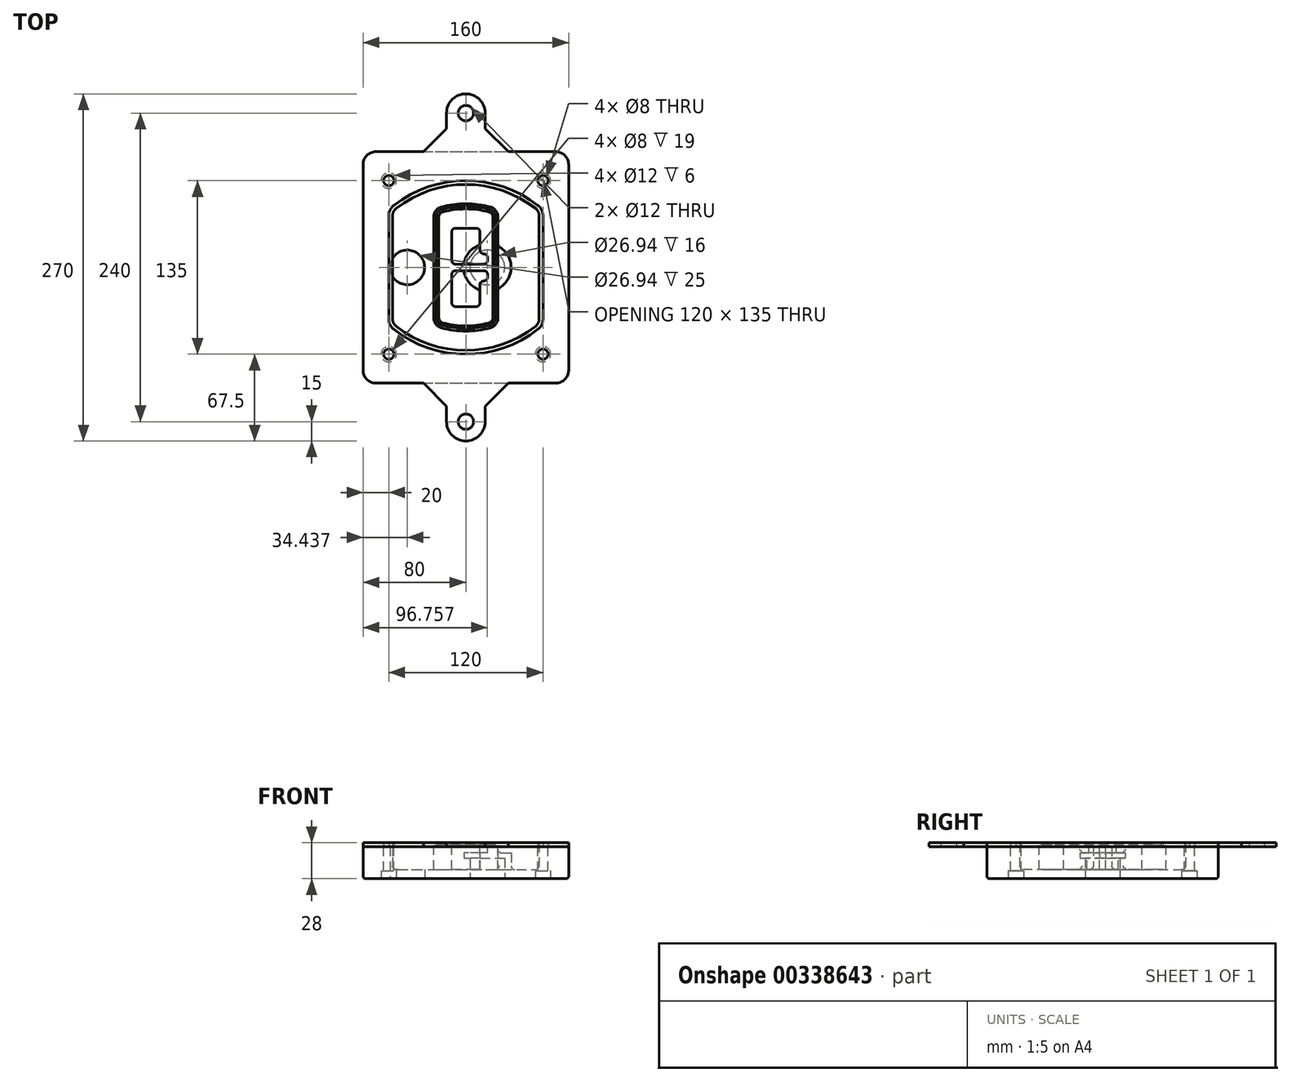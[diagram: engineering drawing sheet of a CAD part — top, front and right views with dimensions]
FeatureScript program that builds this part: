
annotation { "Feature Type Name" : "Feature", "Feature Type Description" : "" }
export const myFeature = defineFeature(function(context is Context, id is Id, definition is map)
    precondition{}
    {
        {
            var Q0;
            Q0=qCreatedBy(makeId("Top.planeOp"),FACE);
            var sketch = newSketch(context, id + "F0", { "sketchPlane" : qUnion([Q0])});
            skPoint(sketch, "E0.rect.middle", {"position": v(0, 0) * mm});
            skLineSegment(sketch, "E1.bottom", {"start": v(-70, -90) * mm, "end": v(70, -90) * mm});
            skLineSegment(sketch, "E1.top", {"start": v(-70, 90) * mm, "end": v(70, 90) * mm});
            skLineSegment(sketch, "E1.left", {"start": v(-80, -80) * mm, "end": v(-80, 80) * mm});
            skLineSegment(sketch, "E1.right", {"start": v(80, -80) * mm, "end": v(80, 80) * mm});
            skLineSegment(sketch, "E2", {"start": v(-80, 90) * mm, "end": v(80, -90) * mm, "construction": true});
            skLineSegment(sketch, "E3", {"start": v(80, 90) * mm, "end": v(-80, -90) * mm, "construction": true});
            skCircle(sketch, "E4", {"center": v(-60, 67.5) * mm, "radius": 4 * mm});
            skCircle(sketch, "E5", {"center": v(60, 67.5) * mm, "radius": 4 * mm});
            skCircle(sketch, "E6", {"center": v(60, -67.5) * mm, "radius": 4 * mm});
            skCircle(sketch, "E7", {"center": v(-60, -67.5) * mm, "radius": 4 * mm});
            skLineSegment(sketch, "E8", {"start": v(-60, 67.5) * mm, "end": v(60, 67.5) * mm, "construction": true});
            skLineSegment(sketch, "E9", {"start": v(60, 67.5) * mm, "end": v(60, -67.5) * mm, "construction": true});
            skLineSegment(sketch, "E10", {"start": v(60, -67.5) * mm, "end": v(-60, -67.5) * mm, "construction": true});
            skLineSegment(sketch, "E11", {"start": v(-60, -67.5) * mm, "end": v(-60, 67.5) * mm, "construction": true});
            skLineSegment(sketch, "E12", {"start": v(-60, 40.3) * mm, "end": v(-60, -40.3) * mm});
            skLineSegment(sketch, "E13", {"start": v(60, 40.3) * mm, "end": v(60, -40.3) * mm});
            skArc(sketch, "E14", {"start": v(56.15, 48.18) * mm, "mid": v(0, 67.5) * mm, "end": v(-56.15, 48.18) * mm});
            skArc(sketch, "E15", {"start": v(-56.15, -48.18) * mm, "mid": v(0, -67.5) * mm, "end": v(56.15, -48.18) * mm});
            skLineSegment(sketch, "E16", {"start": v(-60, 0) * mm, "end": v(60, 0) * mm, "construction": true});
            skPoint(sketch, "E17.visualSharp", {"position": v(-60, -45) * mm});
            skArc(sketch, "E17.filletArc", {"start": v(-60, -40.3) * mm, "mid": v(-58.99, -44.68) * mm, "end": v(-56.15, -48.18) * mm});
            skPoint(sketch, "E18.visualSharp", {"position": v(-60, 45) * mm});
            skArc(sketch, "E18.filletArc", {"start": v(-56.15, 48.18) * mm, "mid": v(-58.99, 44.68) * mm, "end": v(-60, 40.3) * mm});
            skPoint(sketch, "E19.visualSharp", {"position": v(60, 45) * mm});
            skArc(sketch, "E19.filletArc", {"start": v(60, 40.3) * mm, "mid": v(58.99, 44.68) * mm, "end": v(56.15, 48.18) * mm});
            skPoint(sketch, "E20.visualSharp", {"position": v(60, -45) * mm});
            skArc(sketch, "E20.filletArc", {"start": v(56.15, -48.18) * mm, "mid": v(58.99, -44.68) * mm, "end": v(60, -40.3) * mm});
            skPoint(sketch, "E21.visualSharp", {"position": v(-80, 90) * mm});
            skArc(sketch, "E21.filletArc", {"start": v(-70, 90) * mm, "mid": v(-77.07, 87.07) * mm, "end": v(-80, 80) * mm});
            skPoint(sketch, "E22.visualSharp", {"position": v(80, 90) * mm});
            skArc(sketch, "E22.filletArc", {"start": v(80, 80) * mm, "mid": v(77.07, 87.07) * mm, "end": v(70, 90) * mm});
            skPoint(sketch, "E23.visualSharp", {"position": v(80, -90) * mm});
            skArc(sketch, "E23.filletArc", {"start": v(70, -90) * mm, "mid": v(77.07, -87.07) * mm, "end": v(80, -80) * mm});
            skPoint(sketch, "E24.visualSharp", {"position": v(-80, -90) * mm});
            skArc(sketch, "E24.filletArc", {"start": v(-80, -80) * mm, "mid": v(-77.07, -87.07) * mm, "end": v(-70, -90) * mm});
            skArc(sketch, "E25.0", {"start": v(57, 40.3) * mm, "mid": v(56.3, 43.36) * mm, "end": v(54.3, 45.81) * mm});
            skLineSegment(sketch, "E25.1", {"start": v(57, 40.3) * mm, "end": v(57, -40.3) * mm});
            skArc(sketch, "E25.2", {"start": v(54.3, -45.81) * mm, "mid": v(56.3, -43.36) * mm, "end": v(57, -40.3) * mm});
            skArc(sketch, "E25.3", {"start": v(-54.3, -45.81) * mm, "mid": v(0, -64.5) * mm, "end": v(54.3, -45.81) * mm});
            skArc(sketch, "E25.4", {"start": v(-57, -40.3) * mm, "mid": v(-56.3, -43.36) * mm, "end": v(-54.3, -45.81) * mm});
            skArc(sketch, "E25.5", {"start": v(54.3, 45.81) * mm, "mid": v(0, 64.5) * mm, "end": v(-54.3, 45.81) * mm});
            skLineSegment(sketch, "E25.6", {"start": v(-57, 40.3) * mm, "end": v(-57, -40.3) * mm});
            skArc(sketch, "E25.7", {"start": v(-54.3, 45.81) * mm, "mid": v(-56.3, 43.36) * mm, "end": v(-57, 40.3) * mm});
            skArc(sketch, "E26.0", {"start": v(-58.62, 51.33) * mm, "mid": v(-62.58, 46.43) * mm, "end": v(-64, 40.3) * mm});
            skArc(sketch, "E26.1", {"start": v(58.62, 51.33) * mm, "mid": v(0, 71.5) * mm, "end": v(-58.62, 51.33) * mm});
            skArc(sketch, "E26.2", {"start": v(64, 40.3) * mm, "mid": v(62.58, 46.43) * mm, "end": v(58.62, 51.33) * mm});
            skLineSegment(sketch, "E26.3", {"start": v(64, 40.3) * mm, "end": v(64, -40.3) * mm});
            skArc(sketch, "E26.4", {"start": v(58.62, -51.33) * mm, "mid": v(62.58, -46.43) * mm, "end": v(64, -40.3) * mm});
            skLineSegment(sketch, "E26.5", {"start": v(-64, 40.3) * mm, "end": v(-64, -40.3) * mm});
            skArc(sketch, "E26.6", {"start": v(-58.62, -51.33) * mm, "mid": v(0, -71.5) * mm, "end": v(58.62, -51.33) * mm});
            skArc(sketch, "E26.7", {"start": v(-64, -40.3) * mm, "mid": v(-62.58, -46.43) * mm, "end": v(-58.62, -51.33) * mm});
            skSolve(sketch);
        }
        {
            var Q0;
            Q0=makeQuery(id+"F0.imprint","IMPRINT",FACE,{"disambiguationData":[TD([[makeQuery(id+"F0.imprint","IMPRINT",EDGE,{"derivedFrom":sQuery(id+"F0.wireOp",EDGE,"E1.bottom")}),1.0]])]});
            var Q1;
            Q1=makeQuery(id+"F0.imprint","IMPRINT",FACE,{"disambiguationData":[TD([[makeQuery(id+"F0.imprint","IMPRINT",EDGE,{"derivedFrom":sQuery(id+"F0.wireOp",EDGE,"E12")}),1.0]])]});
            var Q2;
            Q2=makeQuery(id+"F0.imprint","IMPRINT",FACE,{"disambiguationData":[TD([[makeQuery(id+"F0.imprint","IMPRINT",EDGE,{"derivedFrom":sQuery(id+"F0.wireOp",EDGE,"E25.0")}),1.0]])]});
            var Q3;
            Q3=makeQuery(id+"F0.imprint","IMPRINT",FACE,{"disambiguationData":[TD([[makeQuery(id+"F0.imprint","IMPRINT",EDGE,{"derivedFrom":sQuery(id+"F0.wireOp",EDGE,"E12")}),-1.0]])]});
            extrude(context, id + "F1", {"entities" : qUnion([Q0, Q1, Q2, Q3]), "oppositeDirection" : true, "depth" : 25 * mm});
        }
        {
            var Q0;
            Q0=makeQuery(id+"F0.imprint","IMPRINT",FACE,{"disambiguationData":[TD([[makeQuery(id+"F0.imprint","IMPRINT",EDGE,{"derivedFrom":sQuery(id+"F0.wireOp",EDGE,"E12")}),1.0]])]});
            extrude(context, id + "F2", {"entities" : qUnion([Q0]), "operationType" : NewBodyOperationType.ADD, "depth" : 3 * mm});
        }
        {
            var Q0;
            Q0=makeQuery(id+"F0.imprint","IMPRINT",FACE,{"disambiguationData":[TD([[makeQuery(id+"F0.imprint","IMPRINT",EDGE,{"derivedFrom":sQuery(id+"F0.wireOp",EDGE,"E25.0")}),1.0]])]});
            extrude(context, id + "F3", {"entities" : qUnion([Q0]), "operationType" : NewBodyOperationType.REMOVE, "oppositeDirection" : true, "depth" : 18 * mm});
        }
        {
            var Q0;
            Q0=makeQuery(id+"F2.opExtrude","CAP_FACE",FACE,{"disambiguationData":[OSD([sQuery(id+"F0.wireOp",EDGE,"E12"),sQuery(id+"F0.wireOp",EDGE,"E13"),sQuery(id+"F0.wireOp",EDGE,"E14"),sQuery(id+"F0.wireOp",EDGE,"E15"),sQuery(id+"F0.wireOp",EDGE,"E17.filletArc"),sQuery(id+"F0.wireOp",EDGE,"E18.filletArc"),sQuery(id+"F0.wireOp",EDGE,"E19.filletArc"),sQuery(id+"F0.wireOp",EDGE,"E20.filletArc"),sQuery(id+"F0.wireOp",EDGE,"E25.0"),sQuery(id+"F0.wireOp",EDGE,"E25.1"),sQuery(id+"F0.wireOp",EDGE,"E25.2"),sQuery(id+"F0.wireOp",EDGE,"E25.3"),sQuery(id+"F0.wireOp",EDGE,"E25.4"),sQuery(id+"F0.wireOp",EDGE,"E25.5"),sQuery(id+"F0.wireOp",EDGE,"E25.6"),sQuery(id+"F0.wireOp",EDGE,"E25.7")])],"isStart":false});
            var sketch = newSketch(context, id + "F4", { "sketchPlane" : qUnion([Q0])});
            skArc(sketch, "E27.0", {"start": v(-19.08, -46.97) * mm, "mid": v(0, -49.5) * mm, "end": v(19.08, -46.97) * mm});
            skArc(sketch, "E28.0", {"start": v(19.08, 46.97) * mm, "mid": v(0, 49.5) * mm, "end": v(-19.08, 46.97) * mm});
            skLineSegment(sketch, "E29", {"start": v(-25, 39.25) * mm, "end": v(-25, -39.25) * mm});
            skLineSegment(sketch, "E30", {"start": v(25, 39.25) * mm, "end": v(25, -39.25) * mm});
            skLineSegment(sketch, "E31", {"start": v(-25, 45.1) * mm, "end": v(25, 45.1) * mm, "construction": true});
            skLineSegment(sketch, "E32", {"start": v(-25, -45.1) * mm, "end": v(25, -45.1) * mm, "construction": true});
            skPoint(sketch, "E33.visualSharp", {"position": v(-25, 45.1) * mm});
            skArc(sketch, "E33.filletArc", {"start": v(-19.08, 46.97) * mm, "mid": v(-23.35, 44.11) * mm, "end": v(-25, 39.25) * mm});
            skPoint(sketch, "E34.visualSharp", {"position": v(25, 45.1) * mm});
            skArc(sketch, "E34.filletArc", {"start": v(25, 39.25) * mm, "mid": v(23.35, 44.11) * mm, "end": v(19.08, 46.97) * mm});
            skPoint(sketch, "E35.visualSharp", {"position": v(25, -45.1) * mm});
            skArc(sketch, "E35.filletArc", {"start": v(19.08, -46.97) * mm, "mid": v(23.35, -44.11) * mm, "end": v(25, -39.25) * mm});
            skPoint(sketch, "E36.visualSharp", {"position": v(-25, -45.1) * mm});
            skArc(sketch, "E36.filletArc", {"start": v(-25, -39.25) * mm, "mid": v(-23.35, -44.11) * mm, "end": v(-19.08, -46.97) * mm});
            skArc(sketch, "E37.0", {"start": v(54.3, 45.81) * mm, "mid": v(0, 64.5) * mm, "end": v(-54.3, 45.81) * mm});
            skArc(sketch, "E37.1", {"start": v(-54.3, 45.81) * mm, "mid": v(-56.3, 43.36) * mm, "end": v(-57, 40.3) * mm});
            skLineSegment(sketch, "E37.2", {"start": v(-57, 40.3) * mm, "end": v(-57, -40.3) * mm});
            skArc(sketch, "E37.3", {"start": v(-57, -40.3) * mm, "mid": v(-56.3, -43.36) * mm, "end": v(-54.3, -45.81) * mm});
            skArc(sketch, "E37.4", {"start": v(-54.3, -45.81) * mm, "mid": v(0, -64.5) * mm, "end": v(54.3, -45.81) * mm});
            skArc(sketch, "E37.5", {"start": v(54.3, -45.81) * mm, "mid": v(56.3, -43.36) * mm, "end": v(57, -40.3) * mm});
            skLineSegment(sketch, "E37.6", {"start": v(57, 40.3) * mm, "end": v(57, -40.3) * mm});
            skArc(sketch, "E37.7", {"start": v(57, 40.3) * mm, "mid": v(56.3, 43.36) * mm, "end": v(54.3, 45.81) * mm});
            skLineSegment(sketch, "E38.0", {"start": v(23, 39.25) * mm, "end": v(23, -39.25) * mm});
            skArc(sketch, "E38.1", {"start": v(18.56, -45.04) * mm, "mid": v(21.76, -42.9) * mm, "end": v(23, -39.25) * mm});
            skArc(sketch, "E38.2", {"start": v(-18.56, -45.04) * mm, "mid": v(0, -47.5) * mm, "end": v(18.56, -45.04) * mm});
            skArc(sketch, "E38.3", {"start": v(-23, -39.25) * mm, "mid": v(-21.76, -42.9) * mm, "end": v(-18.56, -45.04) * mm});
            skLineSegment(sketch, "E38.4", {"start": v(-23, 39.25) * mm, "end": v(-23, -39.25) * mm});
            skArc(sketch, "E38.5", {"start": v(23, 39.25) * mm, "mid": v(21.76, 42.9) * mm, "end": v(18.56, 45.04) * mm});
            skArc(sketch, "E38.6", {"start": v(-18.56, 45.04) * mm, "mid": v(-21.76, 42.9) * mm, "end": v(-23, 39.25) * mm});
            skArc(sketch, "E38.7", {"start": v(18.56, 45.04) * mm, "mid": v(0, 47.5) * mm, "end": v(-18.56, 45.04) * mm});
            skArc(sketch, "E39.0", {"start": v(21, 39.25) * mm, "mid": v(20.18, 41.68) * mm, "end": v(18.04, 43.1) * mm});
            skLineSegment(sketch, "E39.1", {"start": v(21, 39.25) * mm, "end": v(21, -39.25) * mm});
            skArc(sketch, "E39.2", {"start": v(18.04, -43.1) * mm, "mid": v(20.18, -41.68) * mm, "end": v(21, -39.25) * mm});
            skArc(sketch, "E39.3", {"start": v(-18.04, -43.1) * mm, "mid": v(0, -45.5) * mm, "end": v(18.04, -43.1) * mm});
            skArc(sketch, "E39.4", {"start": v(-21, -39.25) * mm, "mid": v(-20.18, -41.68) * mm, "end": v(-18.04, -43.1) * mm});
            skArc(sketch, "E39.5", {"start": v(18.04, 43.1) * mm, "mid": v(0, 45.5) * mm, "end": v(-18.04, 43.1) * mm});
            skLineSegment(sketch, "E39.6", {"start": v(-21, 39.25) * mm, "end": v(-21, -39.25) * mm});
            skArc(sketch, "E39.7", {"start": v(-18.04, 43.1) * mm, "mid": v(-20.18, 41.68) * mm, "end": v(-21, 39.25) * mm});
            skLineSegment(sketch, "E40", {"start": v(-25, 0) * mm, "end": v(25, 0) * mm, "construction": true});
            skLineSegment(sketch, "E41", {"start": v(-11, 5.5) * mm, "end": v(-11, 27.5) * mm});
            skLineSegment(sketch, "E42", {"start": v(-8, 30.5) * mm, "end": v(8, 30.5) * mm});
            skLineSegment(sketch, "E43", {"start": v(11, 27.5) * mm, "end": v(11, 13.5) * mm});
            skLineSegment(sketch, "E44", {"start": v(14, 10.5) * mm, "end": v(14, 10.5) * mm});
            skLineSegment(sketch, "E45", {"start": v(17, 7.5) * mm, "end": v(17, 5.5) * mm});
            skLineSegment(sketch, "E46", {"start": v(14, 2.5) * mm, "end": v(-8, 2.5) * mm});
            skPoint(sketch, "E47.visualSharp", {"position": v(-11, 30.5) * mm});
            skArc(sketch, "E47.filletArc", {"start": v(-8, 30.5) * mm, "mid": v(-10.12, 29.62) * mm, "end": v(-11, 27.5) * mm});
            skPoint(sketch, "E48.visualSharp", {"position": v(11, 30.5) * mm});
            skArc(sketch, "E48.filletArc", {"start": v(11, 27.5) * mm, "mid": v(10.12, 29.62) * mm, "end": v(8, 30.5) * mm});
            skPoint(sketch, "E49.visualSharp", {"position": v(11, 10.5) * mm});
            skArc(sketch, "E49.filletArc", {"start": v(11, 13.5) * mm, "mid": v(11.88, 11.38) * mm, "end": v(14, 10.5) * mm});
            skPoint(sketch, "E50.visualSharp", {"position": v(17, 10.5) * mm});
            skArc(sketch, "E50.filletArc", {"start": v(17, 7.5) * mm, "mid": v(16.12, 9.62) * mm, "end": v(14, 10.5) * mm});
            skPoint(sketch, "E51.visualSharp", {"position": v(17, 2.5) * mm});
            skArc(sketch, "E51.filletArc", {"start": v(14, 2.5) * mm, "mid": v(16.12, 3.38) * mm, "end": v(17, 5.5) * mm});
            skPoint(sketch, "E52.visualSharp", {"position": v(-11, 2.5) * mm});
            skArc(sketch, "E52.filletArc", {"start": v(-11, 5.5) * mm, "mid": v(-10.12, 3.38) * mm, "end": v(-8, 2.5) * mm});
            skLineSegment(sketch, "E53.0.MirrorCS", {"start": v(14, -2.5) * mm, "end": v(-8, -2.5) * mm});
            skArc(sketch, "E54.0.MirrorCS", {"start": v(-11, -5.5) * mm, "mid": v(-10.12, -3.38) * mm, "end": v(-8, -2.5) * mm});
            skLineSegment(sketch, "E55.0.MirrorCS", {"start": v(-11, -5.5) * mm, "end": v(-11, -27.5) * mm});
            skArc(sketch, "E56.0.MirrorCS", {"start": v(-8, -30.5) * mm, "mid": v(-10.12, -29.62) * mm, "end": v(-11, -27.5) * mm});
            skLineSegment(sketch, "E57.0.MirrorCS", {"start": v(-8, -30.5) * mm, "end": v(8, -30.5) * mm});
            skArc(sketch, "E58.0.MirrorCS", {"start": v(11, -27.5) * mm, "mid": v(10.12, -29.62) * mm, "end": v(8, -30.5) * mm});
            skLineSegment(sketch, "E59.0.MirrorCS", {"start": v(11, -27.5) * mm, "end": v(11, -13.5) * mm});
            skArc(sketch, "E60.0.MirrorCS", {"start": v(11, -13.5) * mm, "mid": v(11.88, -11.38) * mm, "end": v(14, -10.5) * mm});
            skArc(sketch, "E61.0.MirrorCS", {"start": v(17, -7.5) * mm, "mid": v(16.12, -9.62) * mm, "end": v(14, -10.5) * mm});
            skLineSegment(sketch, "E62.0.MirrorCS", {"start": v(17, -7.5) * mm, "end": v(17, -5.5) * mm});
            skArc(sketch, "E63.0.MirrorCS", {"start": v(14, -2.5) * mm, "mid": v(16.12, -3.38) * mm, "end": v(17, -5.5) * mm});
            skSolve(sketch);
        }
        {
            var Q0;
            Q0=makeQuery(id+"F4.imprint","IMPRINT",FACE,{"disambiguationData":[TD([[makeQuery(id+"F4.imprint","IMPRINT",EDGE,{"derivedFrom":sQuery(id+"F4.wireOp",EDGE,"E27.0")}),1.0]])]});
            var Q1;
            Q1=makeQuery(id+"F4.imprint","IMPRINT",FACE,{"disambiguationData":[TD([[makeQuery(id+"F4.imprint","IMPRINT",EDGE,{"derivedFrom":sQuery(id+"F4.wireOp",EDGE,"E38.0")}),-1.0]])]});
            var Q2;
            Q2=makeQuery(id+"F4.imprint","IMPRINT",FACE,{"disambiguationData":[TD([[makeQuery(id+"F4.imprint","IMPRINT",EDGE,{"derivedFrom":sQuery(id+"F4.wireOp",EDGE,"E39.0")}),1.0]])]});
            extrude(context, id + "F5", {"entities" : qUnion([Q0, Q1, Q2]), "operationType" : NewBodyOperationType.ADD, "endBound" : BoundingType.UP_TO_NEXT, "oppositeDirection" : true, "depth" : 25 * mm});
        }
        {
            var Q0;
            Q0=makeQuery(id+"F4.imprint","IMPRINT",FACE,{"disambiguationData":[TD([[makeQuery(id+"F4.imprint","IMPRINT",EDGE,{"derivedFrom":sQuery(id+"F4.wireOp",EDGE,"E38.0")}),-1.0]])]});
            extrude(context, id + "F6", {"entities" : qUnion([Q0]), "operationType" : NewBodyOperationType.REMOVE, "oppositeDirection" : true, "depth" : 2 * mm});
        }
        {
            var Q0;
            Q0=makeQuery(id+"F1.opExtrude","CAP_FACE",FACE,{"disambiguationData":[OSD([sQuery(id+"F0.wireOp",EDGE,"E1.bottom"),sQuery(id+"F0.wireOp",EDGE,"E1.top"),sQuery(id+"F0.wireOp",EDGE,"E1.left"),sQuery(id+"F0.wireOp",EDGE,"E1.right"),sQuery(id+"F0.wireOp",EDGE,"E4"),sQuery(id+"F0.wireOp",EDGE,"E5"),sQuery(id+"F0.wireOp",EDGE,"E6"),sQuery(id+"F0.wireOp",EDGE,"E7"),sQuery(id+"F0.wireOp",EDGE,"E21.filletArc"),sQuery(id+"F0.wireOp",EDGE,"E22.filletArc"),sQuery(id+"F0.wireOp",EDGE,"E23.filletArc"),sQuery(id+"F0.wireOp",EDGE,"E24.filletArc")])],"isStart":false});
            var sketch = newSketch(context, id + "F7", { "sketchPlane" : qUnion([Q0])});
            skCircle(sketch, "E64", {"center": v(16.76, 0) * mm, "radius": 13.47 * mm});
            skCircle(sketch, "E65", {"center": v(-45.56, 0) * mm, "radius": 13.47 * mm});
            skLineSegment(sketch, "E66", {"start": v(80, 0) * mm, "end": v(-80, 0) * mm});
            skCircle(sketch, "E67", {"center": v(16.76, 0) * mm, "radius": 18.47 * mm});
            skCircle(sketch, "E68", {"center": v(60, -67.5) * mm, "radius": 6 * mm});
            skCircle(sketch, "E69", {"center": v(-60, -67.5) * mm, "radius": 6 * mm});
            skCircle(sketch, "E70", {"center": v(-60, 67.5) * mm, "radius": 6 * mm});
            skCircle(sketch, "E71", {"center": v(60, 67.5) * mm, "radius": 6 * mm});
            skSolve(sketch);
        }
        {
            var Q0;
            {var subQ1=sQuery(id+"F7.wireOp",EDGE,"E66");var subQ4=sQuery(id+"F7.wireOp",EDGE,"E64");var subQ6=makeQuery(id+"F7.imprint","INTERSECT",VERTEX,{"disambiguationData":[OD(0.0)],"derivedFrom":[subQ4,subQ1]});Q0=makeQuery(id+"F7.imprint","IMPRINT",FACE,{"disambiguationData":[TD([[makeQuery(id+"F7.imprint","IMPRINT",EDGE,{"disambiguationData":[TD([[subQ6,-1.0]])],"derivedFrom":subQ4}),-1.0]])]});}
            var Q1;
            {var subQ0=sQuery(id+"F7.wireOp",EDGE,"E66");var subQ1=sQuery(id+"F7.wireOp",EDGE,"E64");var subQ3=makeQuery(id+"F7.imprint","INTERSECT",VERTEX,{"disambiguationData":[OD(0.0)],"derivedFrom":[subQ1,subQ0]});Q1=makeQuery(id+"F7.imprint","IMPRINT",FACE,{"disambiguationData":[TD([[makeQuery(id+"F7.imprint","IMPRINT",EDGE,{"disambiguationData":[TD([[subQ3,-1.0]])],"derivedFrom":subQ1}),1.0]])]});}
            var Q2;
            {var subQ0=sQuery(id+"F7.wireOp",EDGE,"E66");var subQ1=sQuery(id+"F7.wireOp",EDGE,"E64");var subQ3=makeQuery(id+"F7.imprint","INTERSECT",VERTEX,{"disambiguationData":[OD(0.0)],"derivedFrom":[subQ1,subQ0]});Q2=makeQuery(id+"F7.imprint","IMPRINT",FACE,{"disambiguationData":[TD([[makeQuery(id+"F7.imprint","IMPRINT",EDGE,{"disambiguationData":[TD([[subQ3,1.0]])],"derivedFrom":subQ1}),1.0]])]});}
            var Q3;
            {var subQ1=sQuery(id+"F7.wireOp",EDGE,"E66");var subQ4=sQuery(id+"F7.wireOp",EDGE,"E64");var subQ6=makeQuery(id+"F7.imprint","INTERSECT",VERTEX,{"disambiguationData":[OD(0.0)],"derivedFrom":[subQ4,subQ1]});Q3=makeQuery(id+"F7.imprint","IMPRINT",FACE,{"disambiguationData":[TD([[makeQuery(id+"F7.imprint","IMPRINT",EDGE,{"disambiguationData":[TD([[subQ6,1.0]])],"derivedFrom":subQ4}),-1.0]])]});}
            extrude(context, id + "F8", {"entities" : qUnion([Q0, Q1, Q2, Q3]), "operationType" : NewBodyOperationType.ADD, "oppositeDirection" : true, "depth" : 20 * mm});
        }
        {
            var Q0;
            {var subQ0=sQuery(id+"F7.wireOp",EDGE,"E66");var subQ1=sQuery(id+"F7.wireOp",EDGE,"E64");var subQ3=makeQuery(id+"F7.imprint","INTERSECT",VERTEX,{"disambiguationData":[OD(0.0)],"derivedFrom":[subQ1,subQ0]});Q0=makeQuery(id+"F7.imprint","IMPRINT",FACE,{"disambiguationData":[TD([[makeQuery(id+"F7.imprint","IMPRINT",EDGE,{"disambiguationData":[TD([[subQ3,-1.0]])],"derivedFrom":subQ1}),1.0]])]});}
            var Q1;
            {var subQ0=sQuery(id+"F7.wireOp",EDGE,"E66");var subQ1=sQuery(id+"F7.wireOp",EDGE,"E64");var subQ3=makeQuery(id+"F7.imprint","INTERSECT",VERTEX,{"disambiguationData":[OD(0.0)],"derivedFrom":[subQ1,subQ0]});Q1=makeQuery(id+"F7.imprint","IMPRINT",FACE,{"disambiguationData":[TD([[makeQuery(id+"F7.imprint","IMPRINT",EDGE,{"disambiguationData":[TD([[subQ3,1.0]])],"derivedFrom":subQ1}),1.0]])]});}
            extrude(context, id + "F9", {"entities" : qUnion([Q0, Q1]), "operationType" : NewBodyOperationType.REMOVE, "oppositeDirection" : true, "depth" : 16 * mm});
        }
        {
            var Q0;
            {var subQ0=sQuery(id+"F7.wireOp",EDGE,"E66");var subQ1=sQuery(id+"F7.wireOp",EDGE,"E65");var subQ3=makeQuery(id+"F7.imprint","INTERSECT",VERTEX,{"disambiguationData":[OD(0.0)],"derivedFrom":[subQ1,subQ0]});Q0=makeQuery(id+"F7.imprint","IMPRINT",FACE,{"disambiguationData":[TD([[makeQuery(id+"F7.imprint","IMPRINT",EDGE,{"disambiguationData":[TD([[subQ3,-1.0]])],"derivedFrom":subQ1}),1.0]])]});}
            var Q1;
            {var subQ0=sQuery(id+"F7.wireOp",EDGE,"E66");var subQ1=sQuery(id+"F7.wireOp",EDGE,"E65");var subQ3=makeQuery(id+"F7.imprint","INTERSECT",VERTEX,{"disambiguationData":[OD(0.0)],"derivedFrom":[subQ1,subQ0]});Q1=makeQuery(id+"F7.imprint","IMPRINT",FACE,{"disambiguationData":[TD([[makeQuery(id+"F7.imprint","IMPRINT",EDGE,{"disambiguationData":[TD([[subQ3,1.0]])],"derivedFrom":subQ1}),1.0]])]});}
            extrude(context, id + "F10", {"entities" : qUnion([Q0, Q1]), "operationType" : NewBodyOperationType.REMOVE, "oppositeDirection" : true, "depth" : 25 * mm});
        }
        {
            var Q0;
            Q0=makeQuery(id+"F7.imprint","IMPRINT",FACE,{"disambiguationData":[TD([[makeQuery(id+"F7.imprint","IMPRINT",EDGE,{"derivedFrom":sQuery(id+"F7.wireOp",EDGE,"E68")}),1.0]])]});
            var Q1;
            Q1=makeQuery(id+"F7.imprint","IMPRINT",FACE,{"disambiguationData":[TD([[makeQuery(id+"F7.imprint","IMPRINT",EDGE,{"derivedFrom":makeQuery(id+"F1.opExtrude","CAP_EDGE",EDGE,{"disambiguationData":[OSD([sQuery(id+"F0.wireOp",EDGE,"E5")])],"isStart":false})}),-1.0]])]});
            var Q2;
            Q2=makeQuery(id+"F7.imprint","IMPRINT",FACE,{"disambiguationData":[TD([[makeQuery(id+"F7.imprint","IMPRINT",EDGE,{"derivedFrom":sQuery(id+"F7.wireOp",EDGE,"E69")}),1.0]])]});
            var Q3;
            Q3=makeQuery(id+"F7.imprint","IMPRINT",FACE,{"disambiguationData":[TD([[makeQuery(id+"F7.imprint","IMPRINT",EDGE,{"derivedFrom":makeQuery(id+"F1.opExtrude","CAP_EDGE",EDGE,{"disambiguationData":[OSD([sQuery(id+"F0.wireOp",EDGE,"E4")])],"isStart":false})}),-1.0]])]});
            var Q4;
            Q4=makeQuery(id+"F7.imprint","IMPRINT",FACE,{"disambiguationData":[TD([[makeQuery(id+"F7.imprint","IMPRINT",EDGE,{"derivedFrom":sQuery(id+"F7.wireOp",EDGE,"E70")}),1.0]])]});
            var Q5;
            Q5=makeQuery(id+"F7.imprint","IMPRINT",FACE,{"disambiguationData":[TD([[makeQuery(id+"F7.imprint","IMPRINT",EDGE,{"derivedFrom":makeQuery(id+"F1.opExtrude","CAP_EDGE",EDGE,{"disambiguationData":[OSD([sQuery(id+"F0.wireOp",EDGE,"E7")])],"isStart":false})}),-1.0]])]});
            var Q6;
            Q6=makeQuery(id+"F7.imprint","IMPRINT",FACE,{"disambiguationData":[TD([[makeQuery(id+"F7.imprint","IMPRINT",EDGE,{"derivedFrom":sQuery(id+"F7.wireOp",EDGE,"E71")}),1.0]])]});
            var Q7;
            Q7=makeQuery(id+"F7.imprint","IMPRINT",FACE,{"disambiguationData":[TD([[makeQuery(id+"F7.imprint","IMPRINT",EDGE,{"derivedFrom":makeQuery(id+"F1.opExtrude","CAP_EDGE",EDGE,{"disambiguationData":[OSD([sQuery(id+"F0.wireOp",EDGE,"E6")])],"isStart":false})}),-1.0]])]});
            extrude(context, id + "F11", {"entities" : qUnion([Q0, Q1, Q2, Q3, Q4, Q5, Q6, Q7]), "operationType" : NewBodyOperationType.REMOVE, "oppositeDirection" : true, "depth" : 6 * mm});
        }
        {
            var Q0;
            Q0=makeQuery(id+"F9.boolean.opBoolean","COPY",FACE,{"derivedFrom":makeQuery(id+"F9.opExtrude","CAP_FACE",FACE,{"disambiguationData":[OSD([sQuery(id+"F7.wireOp",EDGE,"E64")])],"isStart":false})});
            var sketch = newSketch(context, id + "F12", { "sketchPlane" : qUnion([Q0])});
            skArc(sketch, "E72.0", {"start": v(11, 17.55) * mm, "mid": v(2.57, 11.82) * mm, "end": v(-1.54, 2.5) * mm});
            skArc(sketch, "E72.1", {"start": v(-1.54, -2.5) * mm, "mid": v(2.57, -11.82) * mm, "end": v(11, -17.55) * mm});
            skLineSegment(sketch, "E73", {"start": v(-1.54, -2.5) * mm, "end": v(14, -2.5) * mm});
            skLineSegment(sketch, "E74.0", {"start": v(14, 2.5) * mm, "end": v(-1.54, 2.5) * mm});
            skArc(sketch, "E74.1", {"start": v(14, 2.5) * mm, "mid": v(16.12, 3.38) * mm, "end": v(17, 5.5) * mm});
            skLineSegment(sketch, "E74.2", {"start": v(17, 7.5) * mm, "end": v(17, 5.5) * mm});
            skArc(sketch, "E74.3", {"start": v(17, 7.5) * mm, "mid": v(16.12, 9.62) * mm, "end": v(14, 10.5) * mm});
            skArc(sketch, "E74.4", {"start": v(11, 13.5) * mm, "mid": v(11.88, 11.38) * mm, "end": v(14, 10.5) * mm});
            skLineSegment(sketch, "E74.5", {"start": v(11, 17.55) * mm, "end": v(11, 13.5) * mm});
            skLineSegment(sketch, "E74.7", {"start": v(14, -2.5) * mm, "end": v(-1.54, -2.5) * mm});
            skArc(sketch, "E74.8", {"start": v(14, -2.5) * mm, "mid": v(16.12, -3.38) * mm, "end": v(17, -5.5) * mm});
            skLineSegment(sketch, "E74.9", {"start": v(17, -7.5) * mm, "end": v(17, -5.5) * mm});
            skArc(sketch, "E74.10", {"start": v(17, -7.5) * mm, "mid": v(16.12, -9.62) * mm, "end": v(14, -10.5) * mm});
            skArc(sketch, "E74.11", {"start": v(11, -13.5) * mm, "mid": v(11.88, -11.38) * mm, "end": v(14, -10.5) * mm});
            skLineSegment(sketch, "E74.12", {"start": v(11, -17.55) * mm, "end": v(11, -13.5) * mm});
            skPoint(sketch, "E75.orphan", {"position": v(11, -27.5) * mm});
            skPoint(sketch, "E76.orphan", {"position": v(-8, -2.5) * mm});
            skPoint(sketch, "E77.orphan", {"position": v(-8, 2.5) * mm});
            skPoint(sketch, "E78.orphan", {"position": v(11, 27.5) * mm});
            skSolve(sketch);
        }
        {
            var Q0;
            {var subQ7=sQuery(id+"F12.wireOp",EDGE,"E72.0");var subQ14=sQuery(id+"F12.wireOp",EDGE,"E72.1");var subQ16=sQuery(id+"F12.wireOp",EDGE,"E74.1");var subQ18=sQuery(id+"F12.wireOp",EDGE,"E74.8");Q0=qUnion([makeQuery(id+"F12.imprint","IMPRINT",FACE,{"disambiguationData":[TD([[makeQuery(id+"F12.imprint","IMPRINT",EDGE,{"derivedFrom":subQ7}),1.0]])]}),makeQuery(id+"F12.imprint","IMPRINT",FACE,{"disambiguationData":[TD([[makeQuery(id+"F12.imprint","IMPRINT",EDGE,{"derivedFrom":subQ14}),1.0]])]}),makeQuery(id+"F12.imprint","IMPRINT",FACE,{"disambiguationData":[TD([[makeQuery(id+"F12.imprint","IMPRINT",EDGE,{"derivedFrom":subQ16}),1.0]])]}),makeQuery(id+"F12.imprint","IMPRINT",FACE,{"disambiguationData":[TD([[makeQuery(id+"F12.imprint","IMPRINT",EDGE,{"derivedFrom":subQ18}),-1.0]])]})]);}
            var Q1;
            Q1=makeQuery(id+"F5.boolean.opBoolean","SPLIT",FACE,{"disambiguationData":[TD([makeQuery(id+"F5.opExtrude","SWEPT_FACE",FACE,{"disambiguationData":[OSD([sQuery(id+"F4.wireOp",EDGE,"E41")])]})])],"derivedFrom":makeQuery(id+"F3.boolean.opBoolean","COPY",FACE,{"derivedFrom":makeQuery(id+"F3.opExtrude","CAP_FACE",FACE,{"disambiguationData":[OSD([sQuery(id+"F0.wireOp",EDGE,"E25.0"),sQuery(id+"F0.wireOp",EDGE,"E25.1"),sQuery(id+"F0.wireOp",EDGE,"E25.2"),sQuery(id+"F0.wireOp",EDGE,"E25.3"),sQuery(id+"F0.wireOp",EDGE,"E25.4"),sQuery(id+"F0.wireOp",EDGE,"E25.5"),sQuery(id+"F0.wireOp",EDGE,"E25.6"),sQuery(id+"F0.wireOp",EDGE,"E25.7")])],"isStart":false})})});
            extrude(context, id + "F13", {"entities" : qUnion([Q0]), "operationType" : NewBodyOperationType.REMOVE, "endBound" : BoundingType.UP_TO_SURFACE, "endBoundEntityFace" : qUnion([Q1]), "depth" : 25 * mm});
        }
        {
            var Q0;
            Q0=makeQuery(id+"F3.boolean.opBoolean","COPY",EDGE,{"derivedFrom":makeQuery(id+"F3.opExtrude","CAP_EDGE",EDGE,{"disambiguationData":[OSD([sQuery(id+"F0.wireOp",EDGE,"E25.6")])],"isStart":false})});
            var Q1;
            Q1=makeQuery(id+"F8.boolean.opBoolean","INTERSECT",EDGE,{"derivedFrom":[makeQuery(id+"F5.opExtrude","SWEPT_FACE",FACE,{"disambiguationData":[OSD([sQuery(id+"F4.wireOp",EDGE,"E30")])]}),makeQuery(id+"F8.opExtrude","CAP_FACE",FACE,{"disambiguationData":[OSD([sQuery(id+"F7.wireOp",EDGE,"E67")])],"isStart":false})]});
            var Q2;
            Q2=makeQuery(id+"F8.boolean.opBoolean","INTERSECT",EDGE,{"disambiguationData":[OD(1.0)],"derivedFrom":[makeQuery(id+"F5.opExtrude","SWEPT_FACE",FACE,{"disambiguationData":[OSD([sQuery(id+"F4.wireOp",EDGE,"E30")])]}),makeQuery(id+"F8.opExtrude","SWEPT_FACE",FACE,{"disambiguationData":[OSD([sQuery(id+"F7.wireOp",EDGE,"E67")])]})]});
            var Q3;
            {var subQ0=makeQuery(id+"F3.boolean.opBoolean","COPY",FACE,{"derivedFrom":makeQuery(id+"F3.opExtrude","CAP_FACE",FACE,{"disambiguationData":[OSD([sQuery(id+"F0.wireOp",EDGE,"E25.0"),sQuery(id+"F0.wireOp",EDGE,"E25.1"),sQuery(id+"F0.wireOp",EDGE,"E25.2"),sQuery(id+"F0.wireOp",EDGE,"E25.3"),sQuery(id+"F0.wireOp",EDGE,"E25.4"),sQuery(id+"F0.wireOp",EDGE,"E25.5"),sQuery(id+"F0.wireOp",EDGE,"E25.6"),sQuery(id+"F0.wireOp",EDGE,"E25.7")])],"isStart":false})});var subQ1=sQuery(id+"F4.wireOp",EDGE,"E30");Q3=makeQuery(id+"F8.boolean.opBoolean","SPLIT",EDGE,{"disambiguationData":[TD([makeQuery(id+"F5.opExtrude","SWEPT_FACE",FACE,{"disambiguationData":[OSD([sQuery(id+"F4.wireOp",EDGE,"E35.filletArc")])]})])],"derivedFrom":makeQuery(id+"F5.opExtrude","TWEAK_EDGE",EDGE,{"derivedFrom":[subQ0,makeQuery(id+"F4.imprint","IMPRINT",EDGE,{"derivedFrom":subQ1})]})});}
            var Q4;
            {var subQ0=sQuery(id+"F0.wireOp",EDGE,"E25.0");var subQ1=sQuery(id+"F0.wireOp",EDGE,"E25.1");var subQ2=sQuery(id+"F0.wireOp",EDGE,"E25.2");var subQ3=sQuery(id+"F0.wireOp",EDGE,"E25.3");var subQ4=sQuery(id+"F0.wireOp",EDGE,"E25.4");var subQ5=sQuery(id+"F0.wireOp",EDGE,"E25.5");var subQ6=sQuery(id+"F0.wireOp",EDGE,"E25.6");var subQ7=sQuery(id+"F0.wireOp",EDGE,"E25.7");Q4=makeQuery(id+"F8.boolean.opBoolean","INTERSECT",EDGE,{"derivedFrom":[makeQuery(id+"F5.boolean.opBoolean","SPLIT",FACE,{"disambiguationData":[TD([makeQuery(id+"F2.opExtrude","SWEPT_FACE",FACE,{"disambiguationData":[OSD([subQ0])]})])],"derivedFrom":makeQuery(id+"F3.boolean.opBoolean","COPY",FACE,{"derivedFrom":makeQuery(id+"F3.opExtrude","CAP_FACE",FACE,{"disambiguationData":[OSD([subQ0,subQ1,subQ2,subQ3,subQ4,subQ5,subQ6,subQ7])],"isStart":false})})}),makeQuery(id+"F8.opExtrude","SWEPT_FACE",FACE,{"disambiguationData":[OSD([sQuery(id+"F7.wireOp",EDGE,"E67")])]})]});}
            var Q5;
            Q5=makeQuery(id+"F8.boolean.opBoolean","INTERSECT",EDGE,{"disambiguationData":[OD(0.0)],"derivedFrom":[makeQuery(id+"F5.opExtrude","SWEPT_FACE",FACE,{"disambiguationData":[OSD([sQuery(id+"F4.wireOp",EDGE,"E30")])]}),makeQuery(id+"F8.opExtrude","SWEPT_FACE",FACE,{"disambiguationData":[OSD([sQuery(id+"F7.wireOp",EDGE,"E67")])]})]});
            fillet(context, id + "F14", {"entities" : qUnion([Q0, Q1, Q2, Q3, Q4, Q5]), "radius" : 3 * mm, "tangentPropagation" : true, "allowEdgeOverflow" : false});
        }
        {
            var Q0;
            Q0=makeQuery(id+"F1.opExtrude","CAP_EDGE",EDGE,{"disambiguationData":[OSD([sQuery(id+"F0.wireOp",EDGE,"E1.bottom")])],"isStart":false});
            fillet(context, id + "F15", {"entities" : qUnion([Q0]), "radius" : 2 * mm, "tangentPropagation" : true, "allowEdgeOverflow" : false});
        }
        {
            var Q0;
            {var subQ0=sQuery(id+"F0.wireOp",EDGE,"E21.filletArc");var subQ1=sQuery(id+"F0.wireOp",EDGE,"E7");var subQ2=sQuery(id+"F0.wireOp",EDGE,"E6");var subQ3=sQuery(id+"F0.wireOp",EDGE,"E5");var subQ4=sQuery(id+"F0.wireOp",EDGE,"E4");var subQ5=sQuery(id+"F0.wireOp",EDGE,"E22.filletArc");var subQ6=sQuery(id+"F0.wireOp",EDGE,"E1.bottom");var subQ7=sQuery(id+"F0.wireOp",EDGE,"E1.right");var subQ8=sQuery(id+"F0.wireOp",EDGE,"E1.top");var subQ9=sQuery(id+"F0.wireOp",EDGE,"E1.left");var subQ10=sQuery(id+"F0.wireOp",EDGE,"E23.filletArc");var subQ11=sQuery(id+"F0.wireOp",EDGE,"E24.filletArc");Q0=makeQuery(id+"F2.boolean.opBoolean","SPLIT",FACE,{"disambiguationData":[TD([makeQuery(id+"F1.opExtrude","SWEPT_FACE",FACE,{"disambiguationData":[OSD([subQ6])]})])],"derivedFrom":makeQuery(id+"F1.opExtrude","CAP_FACE",FACE,{"disambiguationData":[OSD([subQ6,subQ8,subQ9,subQ7,subQ4,subQ3,subQ2,subQ1,subQ0,subQ5,subQ10,subQ11])],"isStart":true})});}
            var sketch = newSketch(context, id + "F16", { "sketchPlane" : qUnion([Q0])});
            skArc(sketch, "E79.0", {"start": v(-70, 90) * mm, "mid": v(-77.07, 87.07) * mm, "end": v(-80, 80) * mm});
            skLineSegment(sketch, "E79.1", {"start": v(-80, -80) * mm, "end": v(-80, 80) * mm});
            skLineSegment(sketch, "E79.2", {"start": v(-70, 90) * mm, "end": v(70, 90) * mm});
            skArc(sketch, "E79.3", {"start": v(80, 80) * mm, "mid": v(77.07, 87.07) * mm, "end": v(70, 90) * mm});
            skLineSegment(sketch, "E79.4", {"start": v(80, -80) * mm, "end": v(80, 80) * mm});
            skCircle(sketch, "E80.0", {"center": v(60, 67.5) * mm, "radius": 4 * mm});
            skCircle(sketch, "E80.1", {"center": v(-60, 67.5) * mm, "radius": 4 * mm});
            skCircle(sketch, "E80.2", {"center": v(-60, -67.5) * mm, "radius": 4 * mm});
            skCircle(sketch, "E80.3", {"center": v(60, -67.5) * mm, "radius": 4 * mm});
            skArc(sketch, "E80.4", {"start": v(-56.15, -48.18) * mm, "mid": v(0, -67.5) * mm, "end": v(56.15, -48.18) * mm});
            skArc(sketch, "E80.5", {"start": v(56.15, -48.18) * mm, "mid": v(58.99, -44.68) * mm, "end": v(60, -40.3) * mm});
            skLineSegment(sketch, "E80.6", {"start": v(60, 40.3) * mm, "end": v(60, -40.3) * mm});
            skArc(sketch, "E80.7", {"start": v(60, 40.3) * mm, "mid": v(58.99, 44.68) * mm, "end": v(56.15, 48.18) * mm});
            skArc(sketch, "E80.8", {"start": v(56.15, 48.18) * mm, "mid": v(0, 67.5) * mm, "end": v(-56.15, 48.18) * mm});
            skArc(sketch, "E80.9", {"start": v(-56.15, 48.18) * mm, "mid": v(-58.99, 44.68) * mm, "end": v(-60, 40.3) * mm});
            skLineSegment(sketch, "E80.10", {"start": v(-60, 40.3) * mm, "end": v(-60, -40.3) * mm});
            skArc(sketch, "E80.11", {"start": v(-60, -40.3) * mm, "mid": v(-58.99, -44.68) * mm, "end": v(-56.15, -48.18) * mm});
            skArc(sketch, "E80.13", {"start": v(-80, -80) * mm, "mid": v(-77.07, -87.07) * mm, "end": v(-70, -90) * mm});
            skLineSegment(sketch, "E80.14", {"start": v(-70, -90) * mm, "end": v(70, -90) * mm});
            skArc(sketch, "E80.15", {"start": v(70, -90) * mm, "mid": v(77.07, -87.07) * mm, "end": v(80, -80) * mm});
            skLineSegment(sketch, "E81", {"start": v(0, 90) * mm, "end": v(0, 120) * mm, "construction": true});
            skCircle(sketch, "E82", {"center": v(0, 120) * mm, "radius": 6 * mm});
            skLineSegment(sketch, "E83", {"start": v(33, 90) * mm, "end": v(15, 108) * mm});
            skLineSegment(sketch, "E84.MirrorCS", {"start": v(-33, 90) * mm, "end": v(-15, 108) * mm});
            skArc(sketch, "E85", {"start": v(0, 135) * mm, "mid": v(-10.6, 130.6) * mm, "end": v(-15, 120) * mm});
            skArc(sketch, "E86.MirrorCS", {"start": v(0, 135) * mm, "mid": v(10.6, 130.6) * mm, "end": v(15, 120) * mm});
            skLineSegment(sketch, "E87", {"start": v(-15, 108) * mm, "end": v(-15, 120) * mm});
            skLineSegment(sketch, "E88", {"start": v(15, 92.3) * mm, "end": v(15, 120) * mm});
            skLineSegment(sketch, "E89", {"start": v(-80, 0) * mm, "end": v(80, 0) * mm, "construction": true});
            skLineSegment(sketch, "E90.MirrorCS", {"start": v(15, 108) * mm, "end": v(15, 120) * mm});
            skLineSegment(sketch, "E91.MirrorCS", {"start": v(-33, -90) * mm, "end": v(-15, -108) * mm});
            skLineSegment(sketch, "E92.MirrorCS", {"start": v(-15, -108) * mm, "end": v(-15, -120) * mm});
            skArc(sketch, "E93.MirrorCS", {"start": v(0, -135) * mm, "mid": v(-10.6, -130.6) * mm, "end": v(-15, -120) * mm});
            skArc(sketch, "E94.MirrorCS", {"start": v(0, -135) * mm, "mid": v(10.6, -130.6) * mm, "end": v(15, -120) * mm});
            skCircle(sketch, "E95.MirrorC", {"center": v(0, -120) * mm, "radius": 6 * mm});
            skLineSegment(sketch, "E96.MirrorCS", {"start": v(0, -90) * mm, "end": v(0, -120) * mm, "construction": true});
            skLineSegment(sketch, "E97.MirrorCS", {"start": v(15, -108) * mm, "end": v(15, -120) * mm});
            skLineSegment(sketch, "E98.MirrorCS", {"start": v(33, -90) * mm, "end": v(15, -108) * mm});
            skSolve(sketch);
        }
        {
            var Q0;
            Q0=makeQuery(id+"F16.imprint","IMPRINT",FACE,{"disambiguationData":[TD([[makeQuery(id+"F16.imprint","IMPRINT",EDGE,{"derivedFrom":sQuery(id+"F16.wireOp",EDGE,"E82")}),-1.0]])]});
            var Q1;
            {var subQ0=sQuery(id+"F16.wireOp",EDGE,"E91.MirrorCS");Q1=makeQuery(id+"F16.imprint","IMPRINT",FACE,{"disambiguationData":[TD([[makeQuery(id+"F16.imprint","IMPRINT",EDGE,{"derivedFrom":subQ0}),1.0]])]});}
            var Q2;
            {var subQ7=sQuery(id+"F16.wireOp",EDGE,"E79.0");Q2=makeQuery(id+"F16.imprint","IMPRINT",FACE,{"disambiguationData":[TD([[makeQuery(id+"F16.imprint","IMPRINT",EDGE,{"derivedFrom":subQ7}),1.0]])]});}
            var Q3;
            Q3=makeQuery(id+"F2.opExtrude","CAP_FACE",FACE,{"disambiguationData":[OSD([sQuery(id+"F0.wireOp",EDGE,"E12"),sQuery(id+"F0.wireOp",EDGE,"E13"),sQuery(id+"F0.wireOp",EDGE,"E14"),sQuery(id+"F0.wireOp",EDGE,"E15"),sQuery(id+"F0.wireOp",EDGE,"E17.filletArc"),sQuery(id+"F0.wireOp",EDGE,"E18.filletArc"),sQuery(id+"F0.wireOp",EDGE,"E19.filletArc"),sQuery(id+"F0.wireOp",EDGE,"E20.filletArc"),sQuery(id+"F0.wireOp",EDGE,"E25.0"),sQuery(id+"F0.wireOp",EDGE,"E25.1"),sQuery(id+"F0.wireOp",EDGE,"E25.2"),sQuery(id+"F0.wireOp",EDGE,"E25.3"),sQuery(id+"F0.wireOp",EDGE,"E25.4"),sQuery(id+"F0.wireOp",EDGE,"E25.5"),sQuery(id+"F0.wireOp",EDGE,"E25.6"),sQuery(id+"F0.wireOp",EDGE,"E25.7")])],"isStart":false});
            extrude(context, id + "F17", {"entities" : qUnion([Q0, Q1, Q2]), "endBound" : BoundingType.UP_TO_SURFACE, "endBoundEntityFace" : qUnion([Q3]), "depth" : 25 * mm});
        }
    });
